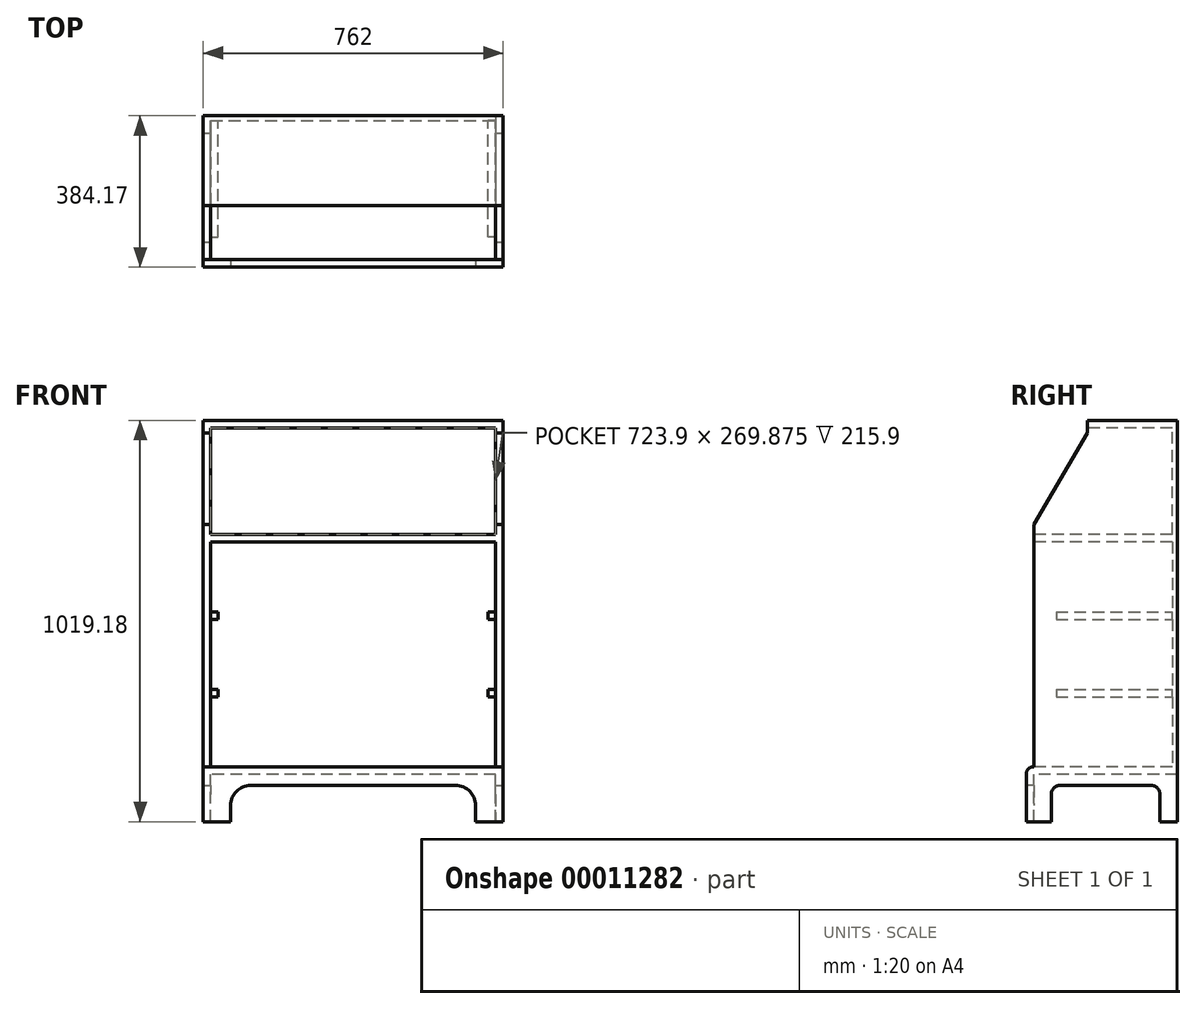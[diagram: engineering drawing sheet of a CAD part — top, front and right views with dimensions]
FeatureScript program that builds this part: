
annotation { "Feature Type Name" : "Feature", "Feature Type Description" : "" }
export const myFeature = defineFeature(function(context is Context, id is Id, definition is map)
    precondition{}
    {
        {
            var Q0;
            Q0=qCreatedBy(makeId("Front.planeOp"),FACE);
            var sketch = newSketch(context, id + "F0", { "sketchPlane" : qUnion([Q0])});
            skLineSegment(sketch, "E0.rect.bottom", {"start": v(381, -19.05) * mm, "end": v(-381, -19.05) * mm});
            skLineSegment(sketch, "E0.rect.top", {"start": v(381, 590.55) * mm, "end": v(-381, 590.55) * mm});
            skLineSegment(sketch, "E0.rect.left", {"start": v(381, -19.05) * mm, "end": v(381, 590.55) * mm});
            skLineSegment(sketch, "E0.rect.right", {"start": v(-381, -19.05) * mm, "end": v(-381, 590.55) * mm});
            skPoint(sketch, "E0.rect.middle", {"position": v(0, 285.75) * mm});
            skLineSegment(sketch, "E1.0", {"start": v(361.95, 571.5) * mm, "end": v(-361.95, 571.5) * mm, "construction": true});
            skLineSegment(sketch, "E1.1", {"start": v(361.95, 0) * mm, "end": v(361.95, 571.5) * mm, "construction": true});
            skLineSegment(sketch, "E1.2", {"start": v(361.95, 0) * mm, "end": v(-361.95, 0) * mm, "construction": true});
            skLineSegment(sketch, "E1.3", {"start": v(-361.95, 0) * mm, "end": v(-361.95, 571.5) * mm, "construction": true});
            skSolve(sketch);
        }
        {
            var Q0;
            Q0 = qSketchRegion(id + "F0", true);
            extrude(context, id + "F1", {"entities" : qUnion([Q0]), "oppositeDirection" : true, "depth" : 365.12 * mm});
        }
        {
            var Q0;
            Q0=qCreatedBy(makeId("Front.planeOp"),FACE);
            var sketch = newSketch(context, id + "F2", { "sketchPlane" : qUnion([Q0])});
            skLineSegment(sketch, "E2.bottom", {"start": v(-361.95, 571.5) * mm, "end": v(361.95, 571.5) * mm});
            skLineSegment(sketch, "E2.top", {"start": v(-361.95, 0) * mm, "end": v(361.95, 0) * mm});
            skLineSegment(sketch, "E2.left", {"start": v(-361.95, 571.5) * mm, "end": v(-361.95, 0) * mm});
            skLineSegment(sketch, "E2.right", {"start": v(361.95, 571.5) * mm, "end": v(361.95, 0) * mm});
            skSolve(sketch);
        }
        {
            var Q0;
            Q0 = qSketchRegion(id + "F2", true);
            extrude(context, id + "F3", {"entities" : qUnion([Q0]), "operationType" : NewBodyOperationType.REMOVE, "oppositeDirection" : true, "depth" : 352.42 * mm});
        }
        {
            var Q0;
            Q0=qCreatedBy(makeId("Top.planeOp"),FACE);
            var sketch = newSketch(context, id + "F4", { "sketchPlane" : qUnion([Q0])});
            skLineSegment(sketch, "E3", {"start": v(-381, 365.13) * mm, "end": v(-361.95, 365.13) * mm});
            skLineSegment(sketch, "E4", {"start": v(361.95, 365.13) * mm, "end": v(381, 365.13) * mm});
            skLineSegment(sketch, "E5", {"start": v(381, 365.13) * mm, "end": v(381, -19.05) * mm});
            skLineSegment(sketch, "E6", {"start": v(381, -19.05) * mm, "end": v(-381, -19.05) * mm});
            skLineSegment(sketch, "E7", {"start": v(-381, -19.05) * mm, "end": v(-381, 365.13) * mm});
            skLineSegment(sketch, "E8.0", {"start": v(-361.95, 0) * mm, "end": v(-361.95, 365.13) * mm});
            skLineSegment(sketch, "E8.1", {"start": v(361.95, 0) * mm, "end": v(-361.95, 0) * mm});
            skLineSegment(sketch, "E8.2", {"start": v(361.95, 365.13) * mm, "end": v(361.95, 0) * mm});
            skSolve(sketch);
        }
        {
            var Q0;
            Q0 = qSketchRegion(id + "F4", true);
            extrude(context, id + "F5", {"entities" : qUnion([Q0]), "operationType" : NewBodyOperationType.ADD, "oppositeDirection" : true, "depth" : 139.7 * mm});
        }
        {
            var Q0;
            Q0=makeQuery(id+"F5.opExtrude","CAP_EDGE",EDGE,{"disambiguationData":[OSD([sQuery(id+"F4.wireOp",EDGE,"E6")])],"isStart":true});
            fillet(context, id + "F6", {"entities" : qUnion([Q0]), "radius" : 19.05 * mm, "allowEdgeOverflow" : false});
        }
        {
            var Q0;
            Q0=makeQuery(id+"F5.opExtrude","SWEPT_FACE",FACE,{"disambiguationData":[OSD([sQuery(id+"F4.wireOp",EDGE,"E6")])]});
            var sketch = newSketch(context, id + "F7", { "sketchPlane" : qUnion([Q0])});
            skLineSegment(sketch, "E9", {"start": v(-311.15, -139.7) * mm, "end": v(311.15, -139.7) * mm});
            skLineSegment(sketch, "E10", {"start": v(311.15, -139.7) * mm, "end": v(311.15, -98.42) * mm});
            skArc(sketch, "E11", {"start": v(311.15, -98.42) * mm, "mid": v(296.27, -62.5) * mm, "end": v(260.35, -47.62) * mm});
            skLineSegment(sketch, "E12", {"start": v(260.35, -47.62) * mm, "end": v(-260.35, -47.63) * mm});
            skLineSegment(sketch, "E13", {"start": v(-311.15, -139.7) * mm, "end": v(-311.15, -98.43) * mm});
            skArc(sketch, "E14", {"start": v(-311.15, -98.43) * mm, "mid": v(-296.27, -62.5) * mm, "end": v(-260.35, -47.63) * mm});
            skLineSegment(sketch, "E15", {"start": v(-381, -139.7) * mm, "end": v(-311.15, -139.7) * mm, "construction": true});
            skLineSegment(sketch, "E16", {"start": v(311.15, -139.7) * mm, "end": v(381, -139.7) * mm, "construction": true});
            skSolve(sketch);
        }
        {
            var Q0;
            Q0 = qSketchRegion(id + "F7", true);
            extrude(context, id + "F8", {"entities" : qUnion([Q0]), "operationType" : NewBodyOperationType.REMOVE, "endBound" : BoundingType.UP_TO_NEXT, "oppositeDirection" : true, "depth" : 25.4 * mm});
        }
        {
            var Q0;
            Q0=makeQuery(id+"F5.boolean.opBoolean","MERGE",FACE,{"derivedFrom":[makeQuery(id+"F1.opExtrude","SWEPT_FACE",FACE,{"disambiguationData":[OSD([sQuery(id+"F0.wireOp",EDGE,"E0.rect.left")])]}),makeQuery(id+"F5.opExtrude","SWEPT_FACE",FACE,{"disambiguationData":[OSD([sQuery(id+"F4.wireOp",EDGE,"E5")])]})]});
            var sketch = newSketch(context, id + "F9", { "sketchPlane" : qUnion([Q0])});
            skLineSegment(sketch, "E17", {"start": v(44.45, -139.7) * mm, "end": v(44.45, -70.54) * mm});
            skLineSegment(sketch, "E18", {"start": v(67.36, -47.62) * mm, "end": v(297.76, -47.62) * mm});
            skLineSegment(sketch, "E19", {"start": v(320.68, -70.54) * mm, "end": v(320.68, -139.7) * mm});
            skLineSegment(sketch, "E20", {"start": v(320.68, -139.7) * mm, "end": v(44.45, -139.7) * mm});
            skArc(sketch, "E21", {"start": v(67.36, -47.62) * mm, "mid": v(51.16, -54.34) * mm, "end": v(44.45, -70.54) * mm});
            skArc(sketch, "E22", {"start": v(297.76, -47.62) * mm, "mid": v(313.96, -54.34) * mm, "end": v(320.68, -70.54) * mm});
            skSolve(sketch);
        }
        {
            var Q0;
            Q0 = qSketchRegion(id + "F9", true);
            var Q1;
            Q1=makeQuery(id+"F5.boolean.opBoolean","MERGE",FACE,{"derivedFrom":[makeQuery(id+"F1.opExtrude","SWEPT_FACE",FACE,{"disambiguationData":[OSD([sQuery(id+"F0.wireOp",EDGE,"E0.rect.right")])]}),makeQuery(id+"F5.opExtrude","SWEPT_FACE",FACE,{"disambiguationData":[OSD([sQuery(id+"F4.wireOp",EDGE,"E7")])]})]});
            extrude(context, id + "F10", {"entities" : qUnion([Q0]), "operationType" : NewBodyOperationType.REMOVE, "endBound" : BoundingType.UP_TO_SURFACE, "oppositeDirection" : true, "endBoundEntityFace" : qUnion([Q1]), "depth" : 25.4 * mm});
        }
        {
            var Q0;
            Q0=makeQuery(id+"F5.boolean.opBoolean","MERGE",FACE,{"derivedFrom":[makeQuery(id+"F1.opExtrude","SWEPT_FACE",FACE,{"disambiguationData":[OSD([sQuery(id+"F0.wireOp",EDGE,"E0.rect.left")])]}),makeQuery(id+"F5.opExtrude","SWEPT_FACE",FACE,{"disambiguationData":[OSD([sQuery(id+"F4.wireOp",EDGE,"E5")])]})]});
            var sketch = newSketch(context, id + "F11", { "sketchPlane" : qUnion([Q0])});
            skLineSegment(sketch, "E23", {"start": v(0, 590.55) * mm, "end": v(365.13, 590.55) * mm});
            skLineSegment(sketch, "E24", {"start": v(365.13, 590.55) * mm, "end": v(365.13, 879.48) * mm});
            skLineSegment(sketch, "E25", {"start": v(136.53, 847.73) * mm, "end": v(0, 615.95) * mm});
            skLineSegment(sketch, "E26", {"start": v(0, 615.95) * mm, "end": v(0, 590.55) * mm});
            skLineSegment(sketch, "E27", {"start": v(365.13, 879.48) * mm, "end": v(136.53, 879.48) * mm});
            skLineSegment(sketch, "E28", {"start": v(136.53, 879.48) * mm, "end": v(136.53, 847.73) * mm});
            skSolve(sketch);
        }
        {
            var Q0;
            Q0 = qSketchRegion(id + "F11", true);
            var Q1;
            Q1=makeQuery(id+"F5.boolean.opBoolean","MERGE",FACE,{"derivedFrom":[makeQuery(id+"F1.opExtrude","SWEPT_FACE",FACE,{"disambiguationData":[OSD([sQuery(id+"F0.wireOp",EDGE,"E0.rect.right")])]}),makeQuery(id+"F5.opExtrude","SWEPT_FACE",FACE,{"disambiguationData":[OSD([sQuery(id+"F4.wireOp",EDGE,"E7")])]})]});
            extrude(context, id + "F12", {"entities" : qUnion([Q0]), "operationType" : NewBodyOperationType.ADD, "endBound" : BoundingType.UP_TO_SURFACE, "oppositeDirection" : true, "endBoundEntityFace" : qUnion([Q1]), "depth" : 25.4 * mm});
        }
        {
            var Q0;
            Q0=qCreatedBy(makeId("Front.planeOp"),FACE);
            var sketch = newSketch(context, id + "F13", { "sketchPlane" : qUnion([Q0])});
            skLineSegment(sketch, "E29.rect.bottom", {"start": v(361.95, 590.55) * mm, "end": v(-361.95, 590.55) * mm});
            skLineSegment(sketch, "E29.rect.top", {"start": v(361.95, 860.43) * mm, "end": v(-361.95, 860.43) * mm});
            skLineSegment(sketch, "E29.rect.left", {"start": v(361.95, 590.55) * mm, "end": v(361.95, 860.43) * mm});
            skLineSegment(sketch, "E29.rect.right", {"start": v(-361.95, 590.55) * mm, "end": v(-361.95, 860.43) * mm});
            skPoint(sketch, "E29.rect.middle", {"position": v(0, 725.49) * mm});
            skSolve(sketch);
        }
        {
            var Q0;
            Q0 = qSketchRegion(id + "F13", true);
            extrude(context, id + "F14", {"entities" : qUnion([Q0]), "operationType" : NewBodyOperationType.REMOVE, "oppositeDirection" : true, "depth" : 352.42 * mm});
        }
        {
            var Q0;
            Q0=makeQuery(id+"F3.boolean.opBoolean","COPY",FACE,{"derivedFrom":makeQuery(id+"F3.opExtrude","CAP_FACE",FACE,{"disambiguationData":[OSD([sQuery(id+"F2.wireOp",EDGE,"E2.bottom"),sQuery(id+"F2.wireOp",EDGE,"E2.top"),sQuery(id+"F2.wireOp",EDGE,"E2.left"),sQuery(id+"F2.wireOp",EDGE,"E2.right")])],"isStart":false})});
            var sketch = newSketch(context, id + "F15", { "sketchPlane" : qUnion([Q0])});
            skLineSegment(sketch, "E30.bottom", {"start": v(-361.95, 177.8) * mm, "end": v(-342.9, 177.8) * mm});
            skLineSegment(sketch, "E30.top", {"start": v(-361.95, 196.85) * mm, "end": v(-342.9, 196.85) * mm});
            skLineSegment(sketch, "E30.left", {"start": v(-361.95, 177.8) * mm, "end": v(-361.95, 196.85) * mm});
            skLineSegment(sketch, "E30.right", {"start": v(-342.9, 177.8) * mm, "end": v(-342.9, 196.85) * mm});
            skLineSegment(sketch, "E31.bottom", {"start": v(-361.95, 374.65) * mm, "end": v(-342.9, 374.65) * mm});
            skLineSegment(sketch, "E31.top", {"start": v(-361.95, 393.7) * mm, "end": v(-342.9, 393.7) * mm});
            skLineSegment(sketch, "E31.left", {"start": v(-361.95, 374.65) * mm, "end": v(-361.95, 393.7) * mm});
            skLineSegment(sketch, "E31.right", {"start": v(-342.9, 374.65) * mm, "end": v(-342.9, 393.7) * mm});
            skLineSegment(sketch, "E32.bottom", {"start": v(361.95, 374.65) * mm, "end": v(342.9, 374.65) * mm});
            skLineSegment(sketch, "E32.top", {"start": v(361.95, 393.7) * mm, "end": v(342.9, 393.7) * mm});
            skLineSegment(sketch, "E32.left", {"start": v(361.95, 374.65) * mm, "end": v(361.95, 393.7) * mm});
            skLineSegment(sketch, "E32.right", {"start": v(342.9, 374.65) * mm, "end": v(342.9, 393.7) * mm});
            skLineSegment(sketch, "E33.bottom", {"start": v(361.95, 177.8) * mm, "end": v(342.9, 177.8) * mm});
            skLineSegment(sketch, "E33.top", {"start": v(361.95, 196.85) * mm, "end": v(342.9, 196.85) * mm});
            skLineSegment(sketch, "E33.left", {"start": v(361.95, 177.8) * mm, "end": v(361.95, 196.85) * mm});
            skLineSegment(sketch, "E33.right", {"start": v(342.9, 177.8) * mm, "end": v(342.9, 196.85) * mm});
            skLineSegment(sketch, "E34", {"start": v(-361.95, 0) * mm, "end": v(-361.95, 177.8) * mm, "construction": true});
            skLineSegment(sketch, "E35", {"start": v(-361.95, 196.85) * mm, "end": v(-361.95, 374.65) * mm, "construction": true});
            skLineSegment(sketch, "E36", {"start": v(361.95, 0) * mm, "end": v(361.95, 177.8) * mm, "construction": true});
            skLineSegment(sketch, "E37", {"start": v(361.95, 196.85) * mm, "end": v(361.95, 374.65) * mm, "construction": true});
            skSolve(sketch);
        }
        {
            var Q0;
            Q0 = qSketchRegion(id + "F15", true);
            extrude(context, id + "F16", {"entities" : qUnion([Q0]), "operationType" : NewBodyOperationType.ADD, "depth" : 295.27 * mm});
        }
    });
